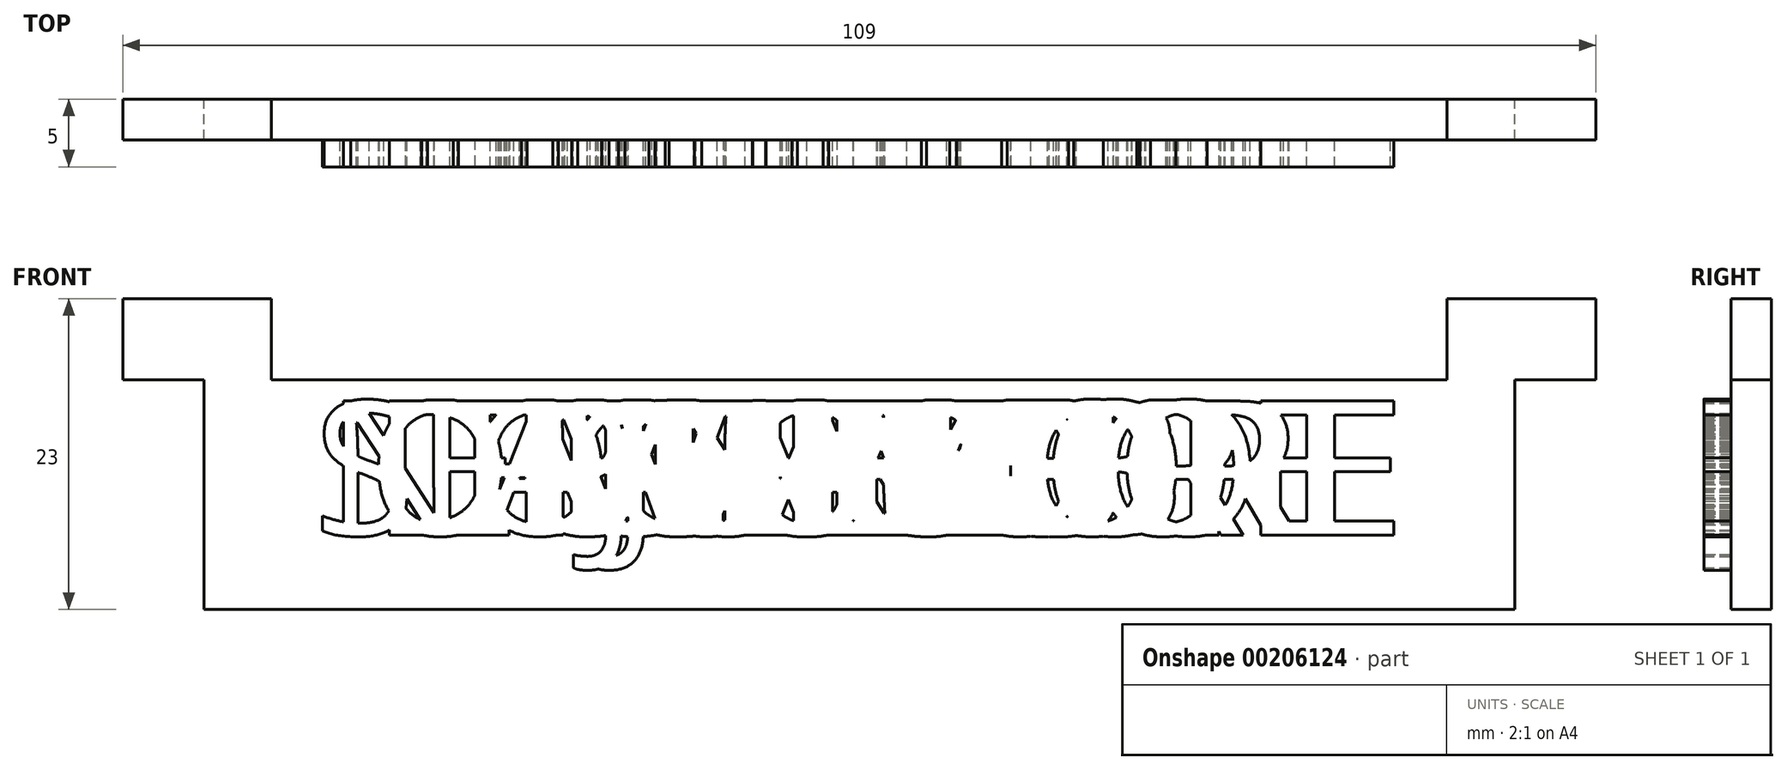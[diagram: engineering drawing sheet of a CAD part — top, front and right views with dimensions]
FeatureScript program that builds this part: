
annotation { "Feature Type Name" : "Feature", "Feature Type Description" : "" }
export const myFeature = defineFeature(function(context is Context, id is Id, definition is map)
    precondition{}
    {
        {
            var Q0;
            Q0=qCreatedBy(makeId("Front.planeOp"),FACE);
            var sketch = newSketch(context, id + "F0", { "sketchPlane" : qUnion([Q0])});
            skLineSegment(sketch, "E0.bottom", {"start": v(-51.5, 23) * mm, "end": v(-40.5, 23) * mm});
            skLineSegment(sketch, "E0.top", {"start": v(-45.5, 0) * mm, "end": v(51.5, 0) * mm});
            skLineSegment(sketch, "E0.left", {"start": v(-51.5, 23) * mm, "end": v(-51.5, 17) * mm});
            skLineSegment(sketch, "E0.right", {"start": v(57.5, 23) * mm, "end": v(57.5, 17) * mm});
            skLineSegment(sketch, "E1.top", {"start": v(-51.5, 17) * mm, "end": v(-45.5, 17) * mm});
            skLineSegment(sketch, "E1.right", {"start": v(-45.5, 0) * mm, "end": v(-45.5, 17) * mm});
            skLineSegment(sketch, "E2.bottom", {"start": v(-51.5, 23) * mm, "end": v(-40.5, 23) * mm, "construction": true});
            skLineSegment(sketch, "E2.top", {"start": v(-51.5, 17) * mm, "end": v(-40.5, 17) * mm, "construction": true});
            skLineSegment(sketch, "E2.left", {"start": v(-51.5, 23) * mm, "end": v(-51.5, 17) * mm, "construction": true});
            skLineSegment(sketch, "E2.right", {"start": v(-40.5, 23) * mm, "end": v(-40.5, 17) * mm, "construction": true});
            skLineSegment(sketch, "E3.top", {"start": v(-40.5, 17) * mm, "end": v(46.5, 17) * mm});
            skLineSegment(sketch, "E3.left", {"start": v(-40.5, 23) * mm, "end": v(-40.5, 17) * mm});
            skLineSegment(sketch, "E3.right", {"start": v(46.5, 23) * mm, "end": v(46.5, 17) * mm});
            skLineSegment(sketch, "E4.top", {"start": v(57.5, 17) * mm, "end": v(51.5, 17) * mm});
            skLineSegment(sketch, "E4.right", {"start": v(51.5, 0) * mm, "end": v(51.5, 17) * mm});
            skLineSegment(sketch, "E5.trimOffspring", {"start": v(46.5, 23) * mm, "end": v(57.5, 23) * mm});
            skSolve(sketch);
        }
        {
            var Q0;
            Q0=makeQuery(id+"F0.imprint","IMPRINT",FACE,{"disambiguationData":[TD([[makeQuery(id+"F0.imprint","IMPRINT",EDGE,{"derivedFrom":sQuery(id+"F0.wireOp",EDGE,"E0.bottom")}),-1.0]])]});
            extrude(context, id + "F1", {"entities" : qUnion([Q0]), "depth" : 3 * mm});
        }
        {
            var Q0;
            Q0=makeQuery(id+"F1.opExtrude","CAP_FACE",FACE,{"disambiguationData":[OSD([sQuery(id+"F0.wireOp",EDGE,"E0.bottom"),sQuery(id+"F0.wireOp",EDGE,"E0.top"),sQuery(id+"F0.wireOp",EDGE,"E0.left"),sQuery(id+"F0.wireOp",EDGE,"E0.right"),sQuery(id+"F0.wireOp",EDGE,"E1.top"),sQuery(id+"F0.wireOp",EDGE,"E1.right"),sQuery(id+"F0.wireOp",EDGE,"E3.top"),sQuery(id+"F0.wireOp",EDGE,"E3.left"),sQuery(id+"F0.wireOp",EDGE,"E3.right"),sQuery(id+"F0.wireOp",EDGE,"E4.top"),sQuery(id+"F0.wireOp",EDGE,"E4.right"),sQuery(id+"F0.wireOp",EDGE,"E5.trimOffspring")])],"isStart":false});
            var sketch = newSketch(context, id + "F2", { "sketchPlane" : qUnion([Q0])});
            skLineSegment(sketch, "E6.0", {"start": v(-45.5, 3.5) * mm, "end": v(-42, 3.5) * mm, "construction": true});
            skLineSegment(sketch, "E7.0", {"start": v(-42, 15.5) * mm, "end": v(48, 15.5) * mm, "construction": true});
            skLineSegment(sketch, "E8.0", {"start": v(-42, 0) * mm, "end": v(-42, 15.5) * mm, "construction": true});
            skText(sketch, "E9", { "text": "ENERO", "fontName": "OpenSans-Regular.ttf"});
            skLineSegment(sketch, "E10.top", {"start": v(-45.5, 0) * mm, "end": v(-42, 0) * mm, "construction": true});
            skLineSegment(sketch, "E10.left", {"start": v(-45.5, 3.5) * mm, "end": v(-45.5, 0) * mm, "construction": true});
            skLineSegment(sketch, "E10.right", {"start": v(-42, 3.5) * mm, "end": v(-42, 0) * mm, "construction": true});
            skLineSegment(sketch, "E11.0", {"start": v(48, 0) * mm, "end": v(48, 17) * mm, "construction": true});
            skPoint(sketch, "E12.orphan", {"position": v(48, 15.5) * mm});
            skPoint(sketch, "E13.end.orphan", {"position": v(3, 0) * mm});
            skLineSegment(sketch, "E14", {"start": v(3, 17) * mm, "end": v(3, 0) * mm, "construction": true});
            const initialGuessF2  = {"E9": [-0.01969, 0.0055, 1, 0, 0.01]};
            skSetInitialGuess(sketch, initialGuessF2);
            skSolve(sketch);
        }
        {
            var Q0;
            Q0=makeQuery(id+"F2.imprint","IMPRINT",FACE,{"disambiguationData":[TD([[makeQuery(id+"F2.imprint","IMPRINT",EDGE,{"derivedFrom":sQuery(id+"F2.wireOp",EDGE,"E9.sketch_text.stroke-0")}),-1.0]])]});
            var Q1;
            Q1=makeQuery(id+"F2.imprint","IMPRINT",FACE,{"disambiguationData":[TD([[makeQuery(id+"F2.imprint","IMPRINT",EDGE,{"derivedFrom":sQuery(id+"F2.wireOp",EDGE,"E9.sketch_text.stroke-10")}),-1.0]])]});
            var Q2;
            Q2=makeQuery(id+"F2.imprint","IMPRINT",FACE,{"disambiguationData":[TD([[makeQuery(id+"F2.imprint","IMPRINT",EDGE,{"derivedFrom":sQuery(id+"F2.wireOp",EDGE,"E9.sketch_text.stroke-23")}),-1.0]])]});
            var Q3;
            Q3=makeQuery(id+"F2.imprint","IMPRINT",FACE,{"disambiguationData":[TD([[makeQuery(id+"F2.imprint","IMPRINT",EDGE,{"derivedFrom":sQuery(id+"F2.wireOp",EDGE,"E9.sketch_text.stroke-38")}),-1.0]])]});
            var Q4;
            Q4=makeQuery(id+"F2.imprint","IMPRINT",FACE,{"disambiguationData":[TD([[makeQuery(id+"F2.imprint","IMPRINT",EDGE,{"derivedFrom":sQuery(id+"F2.wireOp",EDGE,"E9.sketch_text.stroke-52")}),-1.0]])]});
            var Q5;
            Q5=makeQuery(id+"F2.imprint","IMPRINT",FACE,{"disambiguationData":[TD([[makeQuery(id+"F2.imprint","IMPRINT",EDGE,{"derivedFrom":sQuery(id+"F2.wireOp",EDGE,"E9.sketch_text.stroke-65")}),-1.0]])]});
            var Q6;
            Q6=makeQuery(id+"F2.imprint","IMPRINT",FACE,{"disambiguationData":[TD([[makeQuery(id+"F2.imprint","IMPRINT",EDGE,{"derivedFrom":sQuery(id+"F2.wireOp",EDGE,"E9.sketch_text.stroke-83")}),-1.0]])]});
            extrude(context, id + "F3", {"entities" : qUnion([Q0, Q1, Q2, Q3, Q4, Q5, Q6]), "operationType" : NewBodyOperationType.ADD, "depth" : 2 * mm});
        }
        {
            var Q0;
            Q0=qSketchRegion(id+"F0",true);
            extrude(context, id + "F4", {"entities" : qUnion([Q0]), "depth" : 3 * mm});
        }
        {
            var Q0;
            Q0=makeQuery(id+"F4.opExtrude","CAP_FACE",FACE,{"disambiguationData":[OSD([sQuery(id+"F0.wireOp",EDGE,"E0.bottom"),sQuery(id+"F0.wireOp",EDGE,"E0.top"),sQuery(id+"F0.wireOp",EDGE,"E0.left"),sQuery(id+"F0.wireOp",EDGE,"E0.right"),sQuery(id+"F0.wireOp",EDGE,"E1.top"),sQuery(id+"F0.wireOp",EDGE,"E1.right"),sQuery(id+"F0.wireOp",EDGE,"E3.top"),sQuery(id+"F0.wireOp",EDGE,"E3.left"),sQuery(id+"F0.wireOp",EDGE,"E3.right"),sQuery(id+"F0.wireOp",EDGE,"E4.top"),sQuery(id+"F0.wireOp",EDGE,"E4.right"),sQuery(id+"F0.wireOp",EDGE,"E5.trimOffspring")])],"isStart":false});
            var sketch = newSketch(context, id + "F5", { "sketchPlane" : qUnion([Q0])});
            skText(sketch, "E15", { "text": "FEBRERO", "fontName": "OpenSans-Regular.ttf"});
            skPoint(sketch, "E16.orphan", {"position": v(44.22, 15.5) * mm});
            skPoint(sketch, "E17.end.orphan", {"position": v(-0.5, 0) * mm});
            skPoint(sketch, "E18.orphan", {"position": v(-38.22, 15.5) * mm});
            skLineSegment(sketch, "E19.0", {"start": v(-43.5, 15.5) * mm, "end": v(49.5, 15.5) * mm, "construction": true});
            skPoint(sketch, "E20.start.orphan", {"position": v(3, 17) * mm});
            const initialGuessF5  = {"E15": [-0.02683, 0.0055, 1, 0, 0.01]};
            skSetInitialGuess(sketch, initialGuessF5);
            skSolve(sketch);
        }
        {
            var Q0;
            Q0=makeQuery(id+"F5.imprint","IMPRINT",FACE,{"disambiguationData":[TD([[makeQuery(id+"F5.imprint","IMPRINT",EDGE,{"derivedFrom":sQuery(id+"F5.wireOp",EDGE,"E15.sketch_text.stroke-0")}),-1.0]])]});
            var Q1;
            Q1=makeQuery(id+"F5.imprint","IMPRINT",FACE,{"disambiguationData":[TD([[makeQuery(id+"F5.imprint","IMPRINT",EDGE,{"derivedFrom":sQuery(id+"F5.wireOp",EDGE,"E15.sketch_text.stroke-10")}),-1.0]])]});
            var Q2;
            Q2=makeQuery(id+"F5.imprint","IMPRINT",FACE,{"disambiguationData":[TD([[makeQuery(id+"F5.imprint","IMPRINT",EDGE,{"derivedFrom":sQuery(id+"F5.wireOp",EDGE,"E15.sketch_text.stroke-22")}),-1.0]])]});
            var Q3;
            Q3=makeQuery(id+"F5.imprint","IMPRINT",FACE,{"disambiguationData":[TD([[makeQuery(id+"F5.imprint","IMPRINT",EDGE,{"derivedFrom":sQuery(id+"F5.wireOp",EDGE,"E15.sketch_text.stroke-47")}),-1.0]])]});
            var Q4;
            Q4=makeQuery(id+"F5.imprint","IMPRINT",FACE,{"disambiguationData":[TD([[makeQuery(id+"F5.imprint","IMPRINT",EDGE,{"derivedFrom":sQuery(id+"F5.wireOp",EDGE,"E15.sketch_text.stroke-65")}),-1.0]])]});
            var Q5;
            Q5=makeQuery(id+"F5.imprint","IMPRINT",FACE,{"disambiguationData":[TD([[makeQuery(id+"F5.imprint","IMPRINT",EDGE,{"derivedFrom":sQuery(id+"F5.wireOp",EDGE,"E15.sketch_text.stroke-79")}),-1.0]])]});
            var Q6;
            Q6=makeQuery(id+"F5.imprint","IMPRINT",FACE,{"disambiguationData":[TD([[makeQuery(id+"F5.imprint","IMPRINT",EDGE,{"derivedFrom":sQuery(id+"F5.wireOp",EDGE,"E15.sketch_text.stroke-92")}),-1.0]])]});
            var Q7;
            Q7=makeQuery(id+"F5.imprint","IMPRINT",FACE,{"disambiguationData":[TD([[makeQuery(id+"F5.imprint","IMPRINT",EDGE,{"derivedFrom":sQuery(id+"F5.wireOp",EDGE,"E15.sketch_text.stroke-110")}),-1.0]])]});
            extrude(context, id + "F6", {"entities" : qUnion([Q0, Q1, Q2, Q3, Q4, Q5, Q6, Q7]), "operationType" : NewBodyOperationType.ADD, "depth" : 2 * mm});
        }
        {
            var Q0;
            Q0=makeQuery(id+"F0.imprint","IMPRINT",FACE,{"disambiguationData":[TD([[makeQuery(id+"F0.imprint","IMPRINT",EDGE,{"derivedFrom":sQuery(id+"F0.wireOp",EDGE,"E0.bottom")}),-1.0]])]});
            extrude(context, id + "F7", {"entities" : qUnion([Q0]), "depth" : 3 * mm});
        }
        {
            var Q0;
            Q0=makeQuery(id+"F7.opExtrude","CAP_FACE",FACE,{"disambiguationData":[OSD([sQuery(id+"F0.wireOp",EDGE,"E0.bottom"),sQuery(id+"F0.wireOp",EDGE,"E0.top"),sQuery(id+"F0.wireOp",EDGE,"E0.left"),sQuery(id+"F0.wireOp",EDGE,"E0.right"),sQuery(id+"F0.wireOp",EDGE,"E1.top"),sQuery(id+"F0.wireOp",EDGE,"E1.right"),sQuery(id+"F0.wireOp",EDGE,"E3.top"),sQuery(id+"F0.wireOp",EDGE,"E3.left"),sQuery(id+"F0.wireOp",EDGE,"E3.right"),sQuery(id+"F0.wireOp",EDGE,"E4.top"),sQuery(id+"F0.wireOp",EDGE,"E4.right"),sQuery(id+"F0.wireOp",EDGE,"E5.trimOffspring")])],"isStart":false});
            var sketch = newSketch(context, id + "F8", { "sketchPlane" : qUnion([Q0])});
            skText(sketch, "E21", { "text": "MARZO", "fontName": "OpenSans-Regular.ttf"});
            skPoint(sketch, "E22.orphan", {"position": v(38.75, 15.5) * mm});
            skPoint(sketch, "E23.end.orphan", {"position": v(0, -12.7) * mm});
            skPoint(sketch, "E24.orphan", {"position": v(-32.75, 15.5) * mm});
            skPoint(sketch, "E25.start.orphan", {"position": v(0, 4.3) * mm});
            skLineSegment(sketch, "E26.0", {"start": v(-43.5, 15.5) * mm, "end": v(49.5, 15.5) * mm, "construction": true});
            const initialGuessF8  = {"E21": [-0.02136, 0.0055, 1, 0, 0.01]};
            skSetInitialGuess(sketch, initialGuessF8);
            skSolve(sketch);
        }
        {
            var Q0;
            Q0=makeQuery(id+"F8.imprint","IMPRINT",FACE,{"disambiguationData":[TD([[makeQuery(id+"F8.imprint","IMPRINT",EDGE,{"derivedFrom":sQuery(id+"F8.wireOp",EDGE,"E21.sketch_text.stroke-0")}),-1.0]])]});
            var Q1;
            Q1=makeQuery(id+"F8.imprint","IMPRINT",FACE,{"disambiguationData":[TD([[makeQuery(id+"F8.imprint","IMPRINT",EDGE,{"derivedFrom":sQuery(id+"F8.wireOp",EDGE,"E21.sketch_text.stroke-18")}),-1.0]])]});
            var Q2;
            Q2=makeQuery(id+"F8.imprint","IMPRINT",FACE,{"disambiguationData":[TD([[makeQuery(id+"F8.imprint","IMPRINT",EDGE,{"derivedFrom":sQuery(id+"F8.wireOp",EDGE,"E21.sketch_text.stroke-31")}),-1.0]])]});
            var Q3;
            Q3=makeQuery(id+"F8.imprint","IMPRINT",FACE,{"disambiguationData":[TD([[makeQuery(id+"F8.imprint","IMPRINT",EDGE,{"derivedFrom":sQuery(id+"F8.wireOp",EDGE,"E21.sketch_text.stroke-49")}),-1.0]])]});
            var Q4;
            Q4=makeQuery(id+"F8.imprint","IMPRINT",FACE,{"disambiguationData":[TD([[makeQuery(id+"F8.imprint","IMPRINT",EDGE,{"derivedFrom":sQuery(id+"F8.wireOp",EDGE,"E21.sketch_text.stroke-64")}),-1.0]])]});
            extrude(context, id + "F9", {"entities" : qUnion([Q0, Q1, Q2, Q3, Q4]), "operationType" : NewBodyOperationType.ADD, "depth" : 2 * mm});
        }
        {
            var Q0;
            Q0=makeQuery(id+"F0.imprint","IMPRINT",FACE,{"disambiguationData":[TD([[makeQuery(id+"F0.imprint","IMPRINT",EDGE,{"derivedFrom":sQuery(id+"F0.wireOp",EDGE,"E0.bottom")}),-1.0]])]});
            extrude(context, id + "F10", {"entities" : qUnion([Q0]), "depth" : 3 * mm});
        }
        {
            var Q0;
            Q0=makeQuery(id+"F10.opExtrude","CAP_FACE",FACE,{"disambiguationData":[OSD([sQuery(id+"F0.wireOp",EDGE,"E0.bottom"),sQuery(id+"F0.wireOp",EDGE,"E0.top"),sQuery(id+"F0.wireOp",EDGE,"E0.left"),sQuery(id+"F0.wireOp",EDGE,"E0.right"),sQuery(id+"F0.wireOp",EDGE,"E1.top"),sQuery(id+"F0.wireOp",EDGE,"E1.right"),sQuery(id+"F0.wireOp",EDGE,"E3.top"),sQuery(id+"F0.wireOp",EDGE,"E3.left"),sQuery(id+"F0.wireOp",EDGE,"E3.right"),sQuery(id+"F0.wireOp",EDGE,"E4.top"),sQuery(id+"F0.wireOp",EDGE,"E4.right"),sQuery(id+"F0.wireOp",EDGE,"E5.trimOffspring")])],"isStart":false});
            var sketch = newSketch(context, id + "F11", { "sketchPlane" : qUnion([Q0])});
            skText(sketch, "E27", { "text": "ABRIL", "fontName": "OpenSans-Regular.ttf"});
            skPoint(sketch, "E28.orphan", {"position": v(33.4, 15.5) * mm});
            skPoint(sketch, "E29.end.orphan", {"position": v(0.3, -20.32) * mm});
            skPoint(sketch, "E30.orphan", {"position": v(-27.4, 15.5) * mm});
            skPoint(sketch, "E31.start.orphan", {"position": v(0.3, -3.32) * mm});
            skLineSegment(sketch, "E32.0", {"start": v(-43.5, 15.5) * mm, "end": v(49.5, 15.5) * mm});
            const initialGuessF11  = {"E27": [-0.01602, 0.0055, 1, 0, 0.01]};
            skSetInitialGuess(sketch, initialGuessF11);
            skSolve(sketch);
        }
        {
            var Q0;
            Q0=makeQuery(id+"F11.imprint","IMPRINT",FACE,{"disambiguationData":[TD([[makeQuery(id+"F11.imprint","IMPRINT",EDGE,{"derivedFrom":sQuery(id+"F11.wireOp",EDGE,"E27.sketch_text.stroke-0")}),-1.0]])]});
            var Q1;
            Q1=makeQuery(id+"F11.imprint","IMPRINT",FACE,{"disambiguationData":[TD([[makeQuery(id+"F11.imprint","IMPRINT",EDGE,{"derivedFrom":sQuery(id+"F11.wireOp",EDGE,"E27.sketch_text.stroke-13")}),-1.0]])]});
            var Q2;
            Q2=makeQuery(id+"F11.imprint","IMPRINT",FACE,{"disambiguationData":[TD([[makeQuery(id+"F11.imprint","IMPRINT",EDGE,{"derivedFrom":sQuery(id+"F11.wireOp",EDGE,"E27.sketch_text.stroke-28")}),-1.0]])]});
            var Q3;
            Q3=makeQuery(id+"F11.imprint","IMPRINT",FACE,{"disambiguationData":[TD([[makeQuery(id+"F11.imprint","IMPRINT",EDGE,{"derivedFrom":sQuery(id+"F11.wireOp",EDGE,"E27.sketch_text.stroke-46")}),-1.0]])]});
            var Q4;
            Q4=makeQuery(id+"F11.imprint","IMPRINT",FACE,{"disambiguationData":[TD([[makeQuery(id+"F11.imprint","IMPRINT",EDGE,{"derivedFrom":sQuery(id+"F11.wireOp",EDGE,"E27.sketch_text.stroke-50")}),-1.0]])]});
            var Q5;
            Q5=makeQuery(id+"F11.imprint","IMPRINT",FACE,{"disambiguationData":[TD([[makeQuery(id+"F11.imprint","IMPRINT",EDGE,{"derivedFrom":sQuery(id+"F11.wireOp",EDGE,"E27.sketch_text.stroke-56")}),-1.0]])]});
            var Q6;
            Q6=makeQuery(id+"F11.imprint","IMPRINT",FACE,{"disambiguationData":[TD([[makeQuery(id+"F11.imprint","IMPRINT",EDGE,{"derivedFrom":sQuery(id+"F11.wireOp",EDGE,"E27.sketch_text.stroke-60")}),-1.0]])]});
            extrude(context, id + "F12", {"entities" : qUnion([Q0, Q1, Q2, Q3, Q4, Q5, Q6]), "operationType" : NewBodyOperationType.ADD, "depth" : 2 * mm});
        }
        {
            var Q0;
            Q0=makeQuery(id+"F0.imprint","IMPRINT",FACE,{"disambiguationData":[TD([[makeQuery(id+"F0.imprint","IMPRINT",EDGE,{"derivedFrom":sQuery(id+"F0.wireOp",EDGE,"E0.bottom")}),-1.0]])]});
            extrude(context, id + "F13", {"entities" : qUnion([Q0]), "depth" : 3 * mm});
        }
        {
            var Q0;
            Q0=makeQuery(id+"F13.opExtrude","CAP_FACE",FACE,{"disambiguationData":[OSD([sQuery(id+"F0.wireOp",EDGE,"E0.bottom"),sQuery(id+"F0.wireOp",EDGE,"E0.top"),sQuery(id+"F0.wireOp",EDGE,"E0.left"),sQuery(id+"F0.wireOp",EDGE,"E0.right"),sQuery(id+"F0.wireOp",EDGE,"E1.top"),sQuery(id+"F0.wireOp",EDGE,"E1.right"),sQuery(id+"F0.wireOp",EDGE,"E3.top"),sQuery(id+"F0.wireOp",EDGE,"E3.left"),sQuery(id+"F0.wireOp",EDGE,"E3.right"),sQuery(id+"F0.wireOp",EDGE,"E4.top"),sQuery(id+"F0.wireOp",EDGE,"E4.right"),sQuery(id+"F0.wireOp",EDGE,"E5.trimOffspring")])],"isStart":false});
            var sketch = newSketch(context, id + "F14", { "sketchPlane" : qUnion([Q0])});
            skText(sketch, "E33", { "text": "MAYO", "fontName": "OpenSans-Regular.ttf"});
            skPoint(sketch, "E34.orphan", {"position": v(34.38, 15.5) * mm});
            skPoint(sketch, "E35.end.orphan", {"position": v(0.48, -24.9) * mm});
            skPoint(sketch, "E36.orphan", {"position": v(-28.38, 15.5) * mm});
            skPoint(sketch, "E37.start.orphan", {"position": v(0.48, -7.9) * mm});
            skLineSegment(sketch, "E38.0", {"start": v(-41.29, 15.5) * mm, "end": v(47.29, 15.5) * mm});
            skLineSegment(sketch, "E39.0", {"start": v(-43.5, 15.5) * mm, "end": v(49.5, 15.5) * mm});
            const initialGuessF14  = {"E33": [-0.01699, 0.0055, 1, 0, 0.01]};
            skSetInitialGuess(sketch, initialGuessF14);
            skSolve(sketch);
        }
        {
            var Q0;
            Q0=makeQuery(id+"F0.imprint","IMPRINT",FACE,{"disambiguationData":[TD([[makeQuery(id+"F0.imprint","IMPRINT",EDGE,{"derivedFrom":sQuery(id+"F0.wireOp",EDGE,"E0.bottom")}),-1.0]])]});
            extrude(context, id + "F15", {"entities" : qUnion([Q0]), "depth" : 3 * mm});
        }
        {
            var Q0;
            Q0=makeQuery(id+"F15.opExtrude","CAP_FACE",FACE,{"disambiguationData":[OSD([sQuery(id+"F0.wireOp",EDGE,"E0.bottom"),sQuery(id+"F0.wireOp",EDGE,"E0.top"),sQuery(id+"F0.wireOp",EDGE,"E0.left"),sQuery(id+"F0.wireOp",EDGE,"E0.right"),sQuery(id+"F0.wireOp",EDGE,"E1.top"),sQuery(id+"F0.wireOp",EDGE,"E1.right"),sQuery(id+"F0.wireOp",EDGE,"E3.top"),sQuery(id+"F0.wireOp",EDGE,"E3.left"),sQuery(id+"F0.wireOp",EDGE,"E3.right"),sQuery(id+"F0.wireOp",EDGE,"E4.top"),sQuery(id+"F0.wireOp",EDGE,"E4.right"),sQuery(id+"F0.wireOp",EDGE,"E5.trimOffspring")])],"isStart":false});
            var sketch = newSketch(context, id + "F16", { "sketchPlane" : qUnion([Q0])});
            skText(sketch, "E40", { "text": "JUNIO", "fontName": "OpenSans-Regular.ttf"});
            skPoint(sketch, "E41.orphan", {"position": v(34.45, 15.5) * mm});
            skPoint(sketch, "E42.end.orphan", {"position": v(0.65, -29.76) * mm});
            skPoint(sketch, "E43.orphan", {"position": v(-28.45, 15.5) * mm});
            skPoint(sketch, "E44.start.orphan", {"position": v(0.65, -12.76) * mm});
            skLineSegment(sketch, "E45.0", {"start": v(-41.36, 15.5) * mm, "end": v(47.36, 15.5) * mm});
            skLineSegment(sketch, "E46.0", {"start": v(-45.06, 15.5) * mm, "end": v(51.06, 15.5) * mm});
            skLineSegment(sketch, "E47.0", {"start": v(-43.5, 15.5) * mm, "end": v(49.5, 15.5) * mm});
            const initialGuessF16  = {"E40": [-0.01706, 0.0055, 1, 0, 0.01]};
            skSetInitialGuess(sketch, initialGuessF16);
            skSolve(sketch);
        }
        {
            var Q0;
            Q0=makeQuery(id+"F0.imprint","IMPRINT",FACE,{"disambiguationData":[TD([[makeQuery(id+"F0.imprint","IMPRINT",EDGE,{"derivedFrom":sQuery(id+"F0.wireOp",EDGE,"E0.bottom")}),-1.0]])]});
            extrude(context, id + "F17", {"entities" : qUnion([Q0]), "depth" : 3 * mm});
        }
        {
            var Q0;
            Q0=makeQuery(id+"F17.opExtrude","CAP_FACE",FACE,{"disambiguationData":[OSD([sQuery(id+"F0.wireOp",EDGE,"E0.bottom"),sQuery(id+"F0.wireOp",EDGE,"E0.top"),sQuery(id+"F0.wireOp",EDGE,"E0.left"),sQuery(id+"F0.wireOp",EDGE,"E0.right"),sQuery(id+"F0.wireOp",EDGE,"E1.top"),sQuery(id+"F0.wireOp",EDGE,"E1.right"),sQuery(id+"F0.wireOp",EDGE,"E3.top"),sQuery(id+"F0.wireOp",EDGE,"E3.left"),sQuery(id+"F0.wireOp",EDGE,"E3.right"),sQuery(id+"F0.wireOp",EDGE,"E4.top"),sQuery(id+"F0.wireOp",EDGE,"E4.right"),sQuery(id+"F0.wireOp",EDGE,"E5.trimOffspring")])],"isStart":false});
            var sketch = newSketch(context, id + "F18", { "sketchPlane" : qUnion([Q0])});
            skText(sketch, "E48", { "text": "JULIO", "fontName": "OpenSans-Regular.ttf"});
            skPoint(sketch, "E49.orphan", {"position": v(32.82, 15.5) * mm});
            skPoint(sketch, "E50.end.orphan", {"position": v(0.82, -34.76) * mm});
            skPoint(sketch, "E51.orphan", {"position": v(-26.82, 15.5) * mm});
            skPoint(sketch, "E52.start.orphan", {"position": v(0.82, -17.76) * mm});
            skLineSegment(sketch, "E53.0", {"start": v(-39.73, 15.5) * mm, "end": v(45.73, 15.5) * mm});
            skLineSegment(sketch, "E54.0", {"start": v(-43.42, 15.5) * mm, "end": v(49.42, 15.5) * mm});
            skLineSegment(sketch, "E55.0", {"start": v(-41.84, 15.5) * mm, "end": v(47.84, 15.5) * mm});
            skLineSegment(sketch, "E56.0", {"start": v(-43.5, 15.5) * mm, "end": v(49.5, 15.5) * mm});
            const initialGuessF18  = {"E48": [-0.01543, 0.0055, 1, 0, 0.01]};
            skSetInitialGuess(sketch, initialGuessF18);
            skSolve(sketch);
        }
        {
            var Q0;
            Q0=makeQuery(id+"F0.imprint","IMPRINT",FACE,{"disambiguationData":[TD([[makeQuery(id+"F0.imprint","IMPRINT",EDGE,{"derivedFrom":sQuery(id+"F0.wireOp",EDGE,"E0.bottom")}),-1.0]])]});
            extrude(context, id + "F19", {"entities" : qUnion([Q0]), "depth" : 3 * mm});
        }
        {
            var Q0;
            Q0=makeQuery(id+"F19.opExtrude","CAP_FACE",FACE,{"disambiguationData":[OSD([sQuery(id+"F0.wireOp",EDGE,"E0.bottom"),sQuery(id+"F0.wireOp",EDGE,"E0.top"),sQuery(id+"F0.wireOp",EDGE,"E0.left"),sQuery(id+"F0.wireOp",EDGE,"E0.right"),sQuery(id+"F0.wireOp",EDGE,"E1.top"),sQuery(id+"F0.wireOp",EDGE,"E1.right"),sQuery(id+"F0.wireOp",EDGE,"E3.top"),sQuery(id+"F0.wireOp",EDGE,"E3.left"),sQuery(id+"F0.wireOp",EDGE,"E3.right"),sQuery(id+"F0.wireOp",EDGE,"E4.top"),sQuery(id+"F0.wireOp",EDGE,"E4.right"),sQuery(id+"F0.wireOp",EDGE,"E5.trimOffspring")])],"isStart":false});
            var sketch = newSketch(context, id + "F20", { "sketchPlane" : qUnion([Q0])});
            skText(sketch, "E57", { "text": "AGOSTO", "fontName": "OpenSans-Regular.ttf"});
            skPoint(sketch, "E58.orphan", {"position": v(42.34, 15.5) * mm});
            skPoint(sketch, "E59.end.orphan", {"position": v(1, -39.82) * mm});
            skPoint(sketch, "E60.orphan", {"position": v(-36.34, 15.5) * mm});
            skPoint(sketch, "E61.start.orphan", {"position": v(1, -22.82) * mm});
            skLineSegment(sketch, "E62.0", {"start": v(-49.25, 15.5) * mm, "end": v(55.25, 15.5) * mm});
            skLineSegment(sketch, "E63.0", {"start": v(-52.94, 15.5) * mm, "end": v(58.94, 15.5) * mm});
            skLineSegment(sketch, "E64.0", {"start": v(-51.36, 15.5) * mm, "end": v(57.36, 15.5) * mm});
            skLineSegment(sketch, "E65.0", {"start": v(-52.55, 15.5) * mm, "end": v(58.55, 15.5) * mm});
            skLineSegment(sketch, "E66.0", {"start": v(-43.5, 15.5) * mm, "end": v(49.5, 15.5) * mm});
            const initialGuessF20  = {"E57": [-0.02495, 0.0055, 1, 0, 0.01]};
            skSetInitialGuess(sketch, initialGuessF20);
            skSolve(sketch);
        }
        {
            var Q0;
            Q0=makeQuery(id+"F0.imprint","IMPRINT",FACE,{"disambiguationData":[TD([[makeQuery(id+"F0.imprint","IMPRINT",EDGE,{"derivedFrom":sQuery(id+"F0.wireOp",EDGE,"E0.bottom")}),-1.0]])]});
            extrude(context, id + "F21", {"entities" : qUnion([Q0]), "depth" : 3 * mm});
        }
        {
            var Q0;
            Q0=makeQuery(id+"F21.opExtrude","CAP_FACE",FACE,{"disambiguationData":[OSD([sQuery(id+"F0.wireOp",EDGE,"E0.bottom"),sQuery(id+"F0.wireOp",EDGE,"E0.top"),sQuery(id+"F0.wireOp",EDGE,"E0.left"),sQuery(id+"F0.wireOp",EDGE,"E0.right"),sQuery(id+"F0.wireOp",EDGE,"E1.top"),sQuery(id+"F0.wireOp",EDGE,"E1.right"),sQuery(id+"F0.wireOp",EDGE,"E3.top"),sQuery(id+"F0.wireOp",EDGE,"E3.left"),sQuery(id+"F0.wireOp",EDGE,"E3.right"),sQuery(id+"F0.wireOp",EDGE,"E4.top"),sQuery(id+"F0.wireOp",EDGE,"E4.right"),sQuery(id+"F0.wireOp",EDGE,"E5.trimOffspring")])],"isStart":false});
            var sketch = newSketch(context, id + "F22", { "sketchPlane" : qUnion([Q0])});
            skText(sketch, "E67", { "text": "SEPTIEMBRE", "fontName": "OpenSans-Regular.ttf"});
            skPoint(sketch, "E68.orphan", {"position": v(54.84, 15.5) * mm});
            skPoint(sketch, "E69.end.orphan", {"position": v(1.16, -44.91) * mm});
            skPoint(sketch, "E70.orphan", {"position": v(-48.84, 15.5) * mm});
            skPoint(sketch, "E71.start.orphan", {"position": v(1.16, -27.91) * mm});
            const initialGuessF22  = {"E67": [-0.03745, 0.0055, 1, 0, 0.01]};
            skSetInitialGuess(sketch, initialGuessF22);
            skSolve(sketch);
        }
        {
            var Q0;
            Q0=makeQuery(id+"F0.imprint","IMPRINT",FACE,{"disambiguationData":[TD([[makeQuery(id+"F0.imprint","IMPRINT",EDGE,{"derivedFrom":sQuery(id+"F0.wireOp",EDGE,"E0.bottom")}),-1.0]])]});
            extrude(context, id + "F23", {"entities" : qUnion([Q0]), "depth" : 3 * mm});
        }
        {
            var Q0;
            Q0=makeQuery(id+"F23.opExtrude","CAP_FACE",FACE,{"disambiguationData":[OSD([sQuery(id+"F0.wireOp",EDGE,"E0.bottom"),sQuery(id+"F0.wireOp",EDGE,"E0.top"),sQuery(id+"F0.wireOp",EDGE,"E0.left"),sQuery(id+"F0.wireOp",EDGE,"E0.right"),sQuery(id+"F0.wireOp",EDGE,"E1.top"),sQuery(id+"F0.wireOp",EDGE,"E1.right"),sQuery(id+"F0.wireOp",EDGE,"E3.top"),sQuery(id+"F0.wireOp",EDGE,"E3.left"),sQuery(id+"F0.wireOp",EDGE,"E3.right"),sQuery(id+"F0.wireOp",EDGE,"E4.top"),sQuery(id+"F0.wireOp",EDGE,"E4.right"),sQuery(id+"F0.wireOp",EDGE,"E5.trimOffspring")])],"isStart":false});
            var sketch = newSketch(context, id + "F24", { "sketchPlane" : qUnion([Q0])});
            skText(sketch, "E72", { "text": "OCTUBURE", "fontName": "OpenSans-Regular.ttf"});
            skPoint(sketch, "E73.orphan", {"position": v(50.82, 15.5) * mm});
            skPoint(sketch, "E74.end.orphan", {"position": v(1.08, -34.46) * mm});
            skPoint(sketch, "E75.orphan", {"position": v(-44.82, 15.5) * mm});
            skPoint(sketch, "E76.start.orphan", {"position": v(1.08, -17.46) * mm});
            skLineSegment(sketch, "E77.0", {"start": v(-42.5, 15.5) * mm, "end": v(48.5, 15.5) * mm});
            const initialGuessF24  = {"E72": [-0.03343, 0.0055, 1, 0, 0.01]};
            skSetInitialGuess(sketch, initialGuessF24);
            skSolve(sketch);
        }
        {
            var Q0;
            Q0=makeQuery(id+"F0.imprint","IMPRINT",FACE,{"disambiguationData":[TD([[makeQuery(id+"F0.imprint","IMPRINT",EDGE,{"derivedFrom":sQuery(id+"F0.wireOp",EDGE,"E0.bottom")}),-1.0]])]});
            extrude(context, id + "F25", {"entities" : qUnion([Q0]), "depth" : 3 * mm});
        }
        {
            var Q0;
            Q0=makeQuery(id+"F25.opExtrude","CAP_FACE",FACE,{"disambiguationData":[OSD([sQuery(id+"F0.wireOp",EDGE,"E0.bottom"),sQuery(id+"F0.wireOp",EDGE,"E0.top"),sQuery(id+"F0.wireOp",EDGE,"E0.left"),sQuery(id+"F0.wireOp",EDGE,"E0.right"),sQuery(id+"F0.wireOp",EDGE,"E1.top"),sQuery(id+"F0.wireOp",EDGE,"E1.right"),sQuery(id+"F0.wireOp",EDGE,"E3.top"),sQuery(id+"F0.wireOp",EDGE,"E3.left"),sQuery(id+"F0.wireOp",EDGE,"E3.right"),sQuery(id+"F0.wireOp",EDGE,"E4.top"),sQuery(id+"F0.wireOp",EDGE,"E4.right"),sQuery(id+"F0.wireOp",EDGE,"E5.trimOffspring")])],"isStart":false});
            var sketch = newSketch(context, id + "F26", { "sketchPlane" : qUnion([Q0])});
            skText(sketch, "E78", { "text": "NOVIEMBRE", "fontName": "OpenSans-Regular.ttf"});
            skPoint(sketch, "E79.orphan", {"position": v(53.92, 15.5) * mm});
            skPoint(sketch, "E80.end.orphan", {"position": v(1.08, -34.46) * mm});
            skPoint(sketch, "E81.orphan", {"position": v(-47.92, 15.5) * mm});
            skPoint(sketch, "E82.start.orphan", {"position": v(1.08, -17.46) * mm});
            skLineSegment(sketch, "E83.0", {"start": v(-42.5, 15.5) * mm, "end": v(48.5, 15.5) * mm});
            const initialGuessF26  = {"E78": [-0.03653, 0.0055, 1, 0, 0.01]};
            skSetInitialGuess(sketch, initialGuessF26);
            skSolve(sketch);
        }
        {
            var Q0;
            Q0=makeQuery(id+"F0.imprint","IMPRINT",FACE,{"disambiguationData":[TD([[makeQuery(id+"F0.imprint","IMPRINT",EDGE,{"derivedFrom":sQuery(id+"F0.wireOp",EDGE,"E0.bottom")}),-1.0]])]});
            extrude(context, id + "F27", {"entities" : qUnion([Q0]), "depth" : 3 * mm});
        }
        {
            var Q0;
            Q0=makeQuery(id+"F27.opExtrude","CAP_FACE",FACE,{"disambiguationData":[OSD([sQuery(id+"F0.wireOp",EDGE,"E0.bottom"),sQuery(id+"F0.wireOp",EDGE,"E0.top"),sQuery(id+"F0.wireOp",EDGE,"E0.left"),sQuery(id+"F0.wireOp",EDGE,"E0.right"),sQuery(id+"F0.wireOp",EDGE,"E1.top"),sQuery(id+"F0.wireOp",EDGE,"E1.right"),sQuery(id+"F0.wireOp",EDGE,"E3.top"),sQuery(id+"F0.wireOp",EDGE,"E3.left"),sQuery(id+"F0.wireOp",EDGE,"E3.right"),sQuery(id+"F0.wireOp",EDGE,"E4.top"),sQuery(id+"F0.wireOp",EDGE,"E4.right"),sQuery(id+"F0.wireOp",EDGE,"E5.trimOffspring")])],"isStart":false});
            var sketch = newSketch(context, id + "F28", { "sketchPlane" : qUnion([Q0])});
            skText(sketch, "E84", { "text": "DICIEMBRE", "fontName": "OpenSans-Regular.ttf"});
            skPoint(sketch, "E85.orphan", {"position": v(50.53, 15.5) * mm});
            skPoint(sketch, "E86.end.orphan", {"position": v(1.08, -34.46) * mm});
            skPoint(sketch, "E87.orphan", {"position": v(-44.53, 15.5) * mm});
            skPoint(sketch, "E88.start.orphan", {"position": v(1.08, -17.46) * mm});
            skLineSegment(sketch, "E89.0", {"start": v(-42.5, 15.5) * mm, "end": v(48.5, 15.5) * mm});
            const initialGuessF28  = {"E84": [-0.03313, 0.0055, 1, 0, 0.01]};
            skSetInitialGuess(sketch, initialGuessF28);
            skSolve(sketch);
        }
        {
            var Q0;
            Q0=makeQuery(id+"F28.imprint","IMPRINT",FACE,{"disambiguationData":[TD([[makeQuery(id+"F28.imprint","IMPRINT",EDGE,{"derivedFrom":sQuery(id+"F28.wireOp",EDGE,"E84.sketch_text.stroke-0")}),-1.0]])]});
            var Q1;
            Q1=makeQuery(id+"F28.imprint","IMPRINT",FACE,{"disambiguationData":[TD([[makeQuery(id+"F28.imprint","IMPRINT",EDGE,{"derivedFrom":sQuery(id+"F28.wireOp",EDGE,"E84.sketch_text.stroke-14")}),-1.0]])]});
            var Q2;
            Q2=makeQuery(id+"F28.imprint","IMPRINT",FACE,{"disambiguationData":[TD([[makeQuery(id+"F28.imprint","IMPRINT",EDGE,{"derivedFrom":sQuery(id+"F28.wireOp",EDGE,"E84.sketch_text.stroke-26")}),-1.0]])]});
            var Q3;
            Q3=makeQuery(id+"F28.imprint","IMPRINT",FACE,{"disambiguationData":[TD([[makeQuery(id+"F28.imprint","IMPRINT",EDGE,{"derivedFrom":sQuery(id+"F28.wireOp",EDGE,"E84.sketch_text.stroke-41")}),-1.0]])]});
            var Q4;
            Q4=makeQuery(id+"F28.imprint","IMPRINT",FACE,{"disambiguationData":[TD([[makeQuery(id+"F28.imprint","IMPRINT",EDGE,{"derivedFrom":sQuery(id+"F28.wireOp",EDGE,"E84.sketch_text.stroke-53")}),-1.0]])]});
            var Q5;
            Q5=makeQuery(id+"F28.imprint","IMPRINT",FACE,{"disambiguationData":[TD([[makeQuery(id+"F28.imprint","IMPRINT",EDGE,{"derivedFrom":sQuery(id+"F28.wireOp",EDGE,"E84.sketch_text.stroke-71")}),-1.0]])]});
            var Q6;
            Q6=makeQuery(id+"F28.imprint","IMPRINT",FACE,{"disambiguationData":[TD([[makeQuery(id+"F28.imprint","IMPRINT",EDGE,{"derivedFrom":sQuery(id+"F28.wireOp",EDGE,"E84.sketch_text.stroke-96")}),-1.0]])]});
            var Q7;
            Q7=makeQuery(id+"F28.imprint","IMPRINT",FACE,{"disambiguationData":[TD([[makeQuery(id+"F28.imprint","IMPRINT",EDGE,{"derivedFrom":sQuery(id+"F28.wireOp",EDGE,"E84.sketch_text.stroke-108")}),-1.0]])]});
            var Q8;
            Q8=makeQuery(id+"F28.imprint","IMPRINT",FACE,{"disambiguationData":[TD([[makeQuery(id+"F28.imprint","IMPRINT",EDGE,{"derivedFrom":sQuery(id+"F28.wireOp",EDGE,"E84.sketch_text.stroke-33")}),-1.0]])]});
            var Q9;
            Q9=makeQuery(id+"F28.imprint","IMPRINT",FACE,{"disambiguationData":[TD([[makeQuery(id+"F28.imprint","IMPRINT",EDGE,{"derivedFrom":sQuery(id+"F28.wireOp",EDGE,"E84.sketch_text.stroke-110")}),-1.0]])]});
            extrude(context, id + "F29", {"entities" : qUnion([Q0, Q1, Q2, Q3, Q4, Q5, Q6, Q7, Q8, Q9]), "operationType" : NewBodyOperationType.ADD, "depth" : 2 * mm});
        }
        {
            var Q0;
            Q0=makeQuery(id+"F26.imprint","IMPRINT",FACE,{"disambiguationData":[TD([[makeQuery(id+"F26.imprint","IMPRINT",EDGE,{"derivedFrom":sQuery(id+"F26.wireOp",EDGE,"E78.sketch_text.stroke-0")}),-1.0]])]});
            var Q1;
            Q1=makeQuery(id+"F26.imprint","IMPRINT",FACE,{"disambiguationData":[TD([[makeQuery(id+"F26.imprint","IMPRINT",EDGE,{"derivedFrom":sQuery(id+"F26.wireOp",EDGE,"E78.sketch_text.stroke-15")}),-1.0]])]});
            var Q2;
            Q2=makeQuery(id+"F26.imprint","IMPRINT",FACE,{"disambiguationData":[TD([[makeQuery(id+"F26.imprint","IMPRINT",EDGE,{"derivedFrom":sQuery(id+"F26.wireOp",EDGE,"E78.sketch_text.stroke-31")}),-1.0]])]});
            var Q3;
            Q3=makeQuery(id+"F26.imprint","IMPRINT",FACE,{"disambiguationData":[TD([[makeQuery(id+"F26.imprint","IMPRINT",EDGE,{"derivedFrom":sQuery(id+"F26.wireOp",EDGE,"E78.sketch_text.stroke-40")}),-1.0]])]});
            var Q4;
            Q4=makeQuery(id+"F26.imprint","IMPRINT",FACE,{"disambiguationData":[TD([[makeQuery(id+"F26.imprint","IMPRINT",EDGE,{"derivedFrom":sQuery(id+"F26.wireOp",EDGE,"E78.sketch_text.stroke-52")}),-1.0]])]});
            var Q5;
            Q5=makeQuery(id+"F26.imprint","IMPRINT",FACE,{"disambiguationData":[TD([[makeQuery(id+"F26.imprint","IMPRINT",EDGE,{"derivedFrom":sQuery(id+"F26.wireOp",EDGE,"E78.sketch_text.stroke-70")}),-1.0]])]});
            var Q6;
            Q6=makeQuery(id+"F26.imprint","IMPRINT",FACE,{"disambiguationData":[TD([[makeQuery(id+"F26.imprint","IMPRINT",EDGE,{"derivedFrom":sQuery(id+"F26.wireOp",EDGE,"E78.sketch_text.stroke-95")}),-1.0]])]});
            var Q7;
            Q7=makeQuery(id+"F26.imprint","IMPRINT",FACE,{"disambiguationData":[TD([[makeQuery(id+"F26.imprint","IMPRINT",EDGE,{"derivedFrom":sQuery(id+"F26.wireOp",EDGE,"E78.sketch_text.stroke-107")}),-1.0]])]});
            var Q8;
            Q8=makeQuery(id+"F26.imprint","IMPRINT",FACE,{"disambiguationData":[TD([[makeQuery(id+"F26.imprint","IMPRINT",EDGE,{"derivedFrom":sQuery(id+"F26.wireOp",EDGE,"E78.sketch_text.stroke-117")}),-1.0]])]});
            extrude(context, id + "F30", {"entities" : qUnion([Q0, Q1, Q2, Q3, Q4, Q5, Q6, Q7, Q8]), "operationType" : NewBodyOperationType.ADD, "depth" : 2 * mm});
        }
        {
            var Q0;
            Q0=makeQuery(id+"F24.imprint","IMPRINT",FACE,{"disambiguationData":[TD([[makeQuery(id+"F24.imprint","IMPRINT",EDGE,{"derivedFrom":sQuery(id+"F24.wireOp",EDGE,"E72.sketch_text.stroke-0")}),-1.0]])]});
            var Q1;
            Q1=makeQuery(id+"F24.imprint","IMPRINT",FACE,{"disambiguationData":[TD([[makeQuery(id+"F24.imprint","IMPRINT",EDGE,{"derivedFrom":sQuery(id+"F24.wireOp",EDGE,"E72.sketch_text.stroke-16")}),-1.0]])]});
            var Q2;
            Q2=makeQuery(id+"F24.imprint","IMPRINT",FACE,{"disambiguationData":[TD([[makeQuery(id+"F24.imprint","IMPRINT",EDGE,{"derivedFrom":sQuery(id+"F24.wireOp",EDGE,"E72.sketch_text.stroke-31")}),-1.0]])]});
            var Q3;
            Q3=makeQuery(id+"F24.imprint","IMPRINT",FACE,{"disambiguationData":[TD([[makeQuery(id+"F24.imprint","IMPRINT",EDGE,{"derivedFrom":sQuery(id+"F24.wireOp",EDGE,"E72.sketch_text.stroke-39")}),-1.0]])]});
            var Q4;
            Q4=makeQuery(id+"F24.imprint","IMPRINT",FACE,{"disambiguationData":[TD([[makeQuery(id+"F24.imprint","IMPRINT",EDGE,{"derivedFrom":sQuery(id+"F24.wireOp",EDGE,"E72.sketch_text.stroke-55")}),-1.0]])]});
            var Q5;
            Q5=makeQuery(id+"F24.imprint","IMPRINT",FACE,{"disambiguationData":[TD([[makeQuery(id+"F24.imprint","IMPRINT",EDGE,{"derivedFrom":sQuery(id+"F24.wireOp",EDGE,"E72.sketch_text.stroke-80")}),-1.0]])]});
            var Q6;
            Q6=makeQuery(id+"F24.imprint","IMPRINT",FACE,{"disambiguationData":[TD([[makeQuery(id+"F24.imprint","IMPRINT",EDGE,{"derivedFrom":sQuery(id+"F24.wireOp",EDGE,"E72.sketch_text.stroke-92")}),-1.0]])]});
            var Q7;
            Q7=makeQuery(id+"F24.imprint","IMPRINT",FACE,{"disambiguationData":[TD([[makeQuery(id+"F24.imprint","IMPRINT",EDGE,{"derivedFrom":sQuery(id+"F24.wireOp",EDGE,"E72.sketch_text.stroke-110")}),-1.0]])]});
            extrude(context, id + "F31", {"entities" : qUnion([Q0, Q1, Q2, Q3, Q4, Q5, Q6, Q7]), "operationType" : NewBodyOperationType.ADD, "depth" : 2 * mm});
        }
        {
            var Q0;
            Q0=makeQuery(id+"F22.imprint","IMPRINT",FACE,{"disambiguationData":[TD([[makeQuery(id+"F22.imprint","IMPRINT",EDGE,{"derivedFrom":sQuery(id+"F22.wireOp",EDGE,"E67.sketch_text.stroke-0")}),-1.0]])]});
            var Q1;
            Q1=makeQuery(id+"F22.imprint","IMPRINT",FACE,{"disambiguationData":[TD([[makeQuery(id+"F22.imprint","IMPRINT",EDGE,{"derivedFrom":sQuery(id+"F22.wireOp",EDGE,"E67.sketch_text.stroke-25")}),-1.0]])]});
            var Q2;
            Q2=makeQuery(id+"F22.imprint","IMPRINT",FACE,{"disambiguationData":[TD([[makeQuery(id+"F22.imprint","IMPRINT",EDGE,{"derivedFrom":sQuery(id+"F22.wireOp",EDGE,"E67.sketch_text.stroke-37")}),-1.0]])]});
            var Q3;
            Q3=makeQuery(id+"F22.imprint","IMPRINT",FACE,{"disambiguationData":[TD([[makeQuery(id+"F22.imprint","IMPRINT",EDGE,{"derivedFrom":sQuery(id+"F22.wireOp",EDGE,"E67.sketch_text.stroke-52")}),-1.0]])]});
            var Q4;
            Q4=makeQuery(id+"F22.imprint","IMPRINT",FACE,{"disambiguationData":[TD([[makeQuery(id+"F22.imprint","IMPRINT",EDGE,{"derivedFrom":sQuery(id+"F22.wireOp",EDGE,"E67.sketch_text.stroke-60")}),-1.0]])]});
            var Q5;
            Q5=makeQuery(id+"F22.imprint","IMPRINT",FACE,{"disambiguationData":[TD([[makeQuery(id+"F22.imprint","IMPRINT",EDGE,{"derivedFrom":sQuery(id+"F22.wireOp",EDGE,"E67.sketch_text.stroke-72")}),-1.0]])]});
            var Q6;
            Q6=makeQuery(id+"F22.imprint","IMPRINT",FACE,{"disambiguationData":[TD([[makeQuery(id+"F22.imprint","IMPRINT",EDGE,{"derivedFrom":sQuery(id+"F22.wireOp",EDGE,"E67.sketch_text.stroke-90")}),-1.0]])]});
            var Q7;
            Q7=makeQuery(id+"F22.imprint","IMPRINT",FACE,{"disambiguationData":[TD([[makeQuery(id+"F22.imprint","IMPRINT",EDGE,{"derivedFrom":sQuery(id+"F22.wireOp",EDGE,"E67.sketch_text.stroke-115")}),-1.0]])]});
            var Q8;
            Q8=makeQuery(id+"F22.imprint","IMPRINT",FACE,{"disambiguationData":[TD([[makeQuery(id+"F22.imprint","IMPRINT",EDGE,{"derivedFrom":sQuery(id+"F22.wireOp",EDGE,"E67.sketch_text.stroke-127")}),-1.0]])]});
            var Q9;
            Q9=makeQuery(id+"F22.imprint","IMPRINT",FACE,{"disambiguationData":[TD([[makeQuery(id+"F22.imprint","IMPRINT",EDGE,{"derivedFrom":sQuery(id+"F22.wireOp",EDGE,"E67.sketch_text.stroke-137")}),-1.0]])]});
            extrude(context, id + "F32", {"entities" : qUnion([Q0, Q1, Q2, Q3, Q4, Q5, Q6, Q7, Q8, Q9]), "operationType" : NewBodyOperationType.ADD, "depth" : 2 * mm});
        }
        {
            var Q0;
            Q0=makeQuery(id+"F20.imprint","IMPRINT",FACE,{"disambiguationData":[TD([[makeQuery(id+"F20.imprint","IMPRINT",EDGE,{"derivedFrom":sQuery(id+"F20.wireOp",EDGE,"E57.sketch_text.stroke-0")}),-1.0]])]});
            var Q1;
            Q1=makeQuery(id+"F20.imprint","IMPRINT",FACE,{"disambiguationData":[TD([[makeQuery(id+"F20.imprint","IMPRINT",EDGE,{"derivedFrom":sQuery(id+"F20.wireOp",EDGE,"E57.sketch_text.stroke-13")}),-1.0]])]});
            var Q2;
            Q2=makeQuery(id+"F20.imprint","IMPRINT",FACE,{"disambiguationData":[TD([[makeQuery(id+"F20.imprint","IMPRINT",EDGE,{"derivedFrom":sQuery(id+"F20.wireOp",EDGE,"E57.sketch_text.stroke-27")}),-1.0]])]});
            var Q3;
            Q3=makeQuery(id+"F20.imprint","IMPRINT",FACE,{"disambiguationData":[TD([[makeQuery(id+"F20.imprint","IMPRINT",EDGE,{"derivedFrom":sQuery(id+"F20.wireOp",EDGE,"E57.sketch_text.stroke-47")}),-1.0]])]});
            var Q4;
            Q4=makeQuery(id+"F20.imprint","IMPRINT",FACE,{"disambiguationData":[TD([[makeQuery(id+"F20.imprint","IMPRINT",EDGE,{"derivedFrom":sQuery(id+"F20.wireOp",EDGE,"E57.sketch_text.stroke-61")}),-1.0]])]});
            var Q5;
            Q5=makeQuery(id+"F20.imprint","IMPRINT",FACE,{"disambiguationData":[TD([[makeQuery(id+"F20.imprint","IMPRINT",EDGE,{"derivedFrom":sQuery(id+"F20.wireOp",EDGE,"E57.sketch_text.stroke-86")}),-1.0]])]});
            var Q6;
            Q6=makeQuery(id+"F20.imprint","IMPRINT",FACE,{"disambiguationData":[TD([[makeQuery(id+"F20.imprint","IMPRINT",EDGE,{"derivedFrom":sQuery(id+"F20.wireOp",EDGE,"E57.sketch_text.stroke-74")}),-1.0]])]});
            extrude(context, id + "F33", {"entities" : qUnion([Q0, Q1, Q2, Q3, Q4, Q5, Q6]), "operationType" : NewBodyOperationType.ADD, "depth" : 2 * mm});
        }
        {
            var Q0;
            Q0=makeQuery(id+"F18.imprint","IMPRINT",FACE,{"disambiguationData":[TD([[makeQuery(id+"F18.imprint","IMPRINT",EDGE,{"derivedFrom":sQuery(id+"F18.wireOp",EDGE,"E48.sketch_text.stroke-0")}),-1.0]])]});
            var Q1;
            Q1=makeQuery(id+"F18.imprint","IMPRINT",FACE,{"disambiguationData":[TD([[makeQuery(id+"F18.imprint","IMPRINT",EDGE,{"derivedFrom":sQuery(id+"F18.wireOp",EDGE,"E48.sketch_text.stroke-10")}),-1.0]])]});
            var Q2;
            Q2=makeQuery(id+"F18.imprint","IMPRINT",FACE,{"disambiguationData":[TD([[makeQuery(id+"F18.imprint","IMPRINT",EDGE,{"derivedFrom":sQuery(id+"F18.wireOp",EDGE,"E48.sketch_text.stroke-24")}),-1.0]])]});
            var Q3;
            Q3=makeQuery(id+"F18.imprint","IMPRINT",FACE,{"disambiguationData":[TD([[makeQuery(id+"F18.imprint","IMPRINT",EDGE,{"derivedFrom":sQuery(id+"F18.wireOp",EDGE,"E48.sketch_text.stroke-30")}),-1.0]])]});
            var Q4;
            Q4=makeQuery(id+"F18.imprint","IMPRINT",FACE,{"disambiguationData":[TD([[makeQuery(id+"F18.imprint","IMPRINT",EDGE,{"derivedFrom":sQuery(id+"F18.wireOp",EDGE,"E48.sketch_text.stroke-34")}),-1.0]])]});
            extrude(context, id + "F34", {"entities" : qUnion([Q0, Q1, Q2, Q3, Q4]), "operationType" : NewBodyOperationType.ADD, "depth" : 2 * mm});
        }
        {
            var Q0;
            Q0=makeQuery(id+"F16.imprint","IMPRINT",FACE,{"disambiguationData":[TD([[makeQuery(id+"F16.imprint","IMPRINT",EDGE,{"derivedFrom":sQuery(id+"F16.wireOp",EDGE,"E40.sketch_text.stroke-0")}),-1.0]])]});
            var Q1;
            Q1=makeQuery(id+"F16.imprint","IMPRINT",FACE,{"disambiguationData":[TD([[makeQuery(id+"F16.imprint","IMPRINT",EDGE,{"derivedFrom":sQuery(id+"F16.wireOp",EDGE,"E40.sketch_text.stroke-10")}),-1.0]])]});
            var Q2;
            Q2=makeQuery(id+"F16.imprint","IMPRINT",FACE,{"disambiguationData":[TD([[makeQuery(id+"F16.imprint","IMPRINT",EDGE,{"derivedFrom":sQuery(id+"F16.wireOp",EDGE,"E40.sketch_text.stroke-24")}),-1.0]])]});
            var Q3;
            Q3=makeQuery(id+"F16.imprint","IMPRINT",FACE,{"disambiguationData":[TD([[makeQuery(id+"F16.imprint","IMPRINT",EDGE,{"derivedFrom":sQuery(id+"F16.wireOp",EDGE,"E40.sketch_text.stroke-39")}),-1.0]])]});
            var Q4;
            Q4=makeQuery(id+"F16.imprint","IMPRINT",FACE,{"disambiguationData":[TD([[makeQuery(id+"F16.imprint","IMPRINT",EDGE,{"derivedFrom":sQuery(id+"F16.wireOp",EDGE,"E40.sketch_text.stroke-43")}),-1.0]])]});
            extrude(context, id + "F35", {"entities" : qUnion([Q0, Q1, Q2, Q3, Q4]), "operationType" : NewBodyOperationType.ADD, "depth" : 2 * mm});
        }
        {
            var Q0;
            Q0=makeQuery(id+"F14.imprint","IMPRINT",FACE,{"disambiguationData":[TD([[makeQuery(id+"F14.imprint","IMPRINT",EDGE,{"derivedFrom":sQuery(id+"F14.wireOp",EDGE,"E33.sketch_text.stroke-0")}),-1.0]])]});
            var Q1;
            Q1=makeQuery(id+"F14.imprint","IMPRINT",FACE,{"disambiguationData":[TD([[makeQuery(id+"F14.imprint","IMPRINT",EDGE,{"derivedFrom":sQuery(id+"F14.wireOp",EDGE,"E33.sketch_text.stroke-18")}),-1.0]])]});
            var Q2;
            Q2=makeQuery(id+"F14.imprint","IMPRINT",FACE,{"disambiguationData":[TD([[makeQuery(id+"F14.imprint","IMPRINT",EDGE,{"derivedFrom":sQuery(id+"F14.wireOp",EDGE,"E33.sketch_text.stroke-31")}),-1.0]])]});
            var Q3;
            Q3=makeQuery(id+"F14.imprint","IMPRINT",FACE,{"disambiguationData":[TD([[makeQuery(id+"F14.imprint","IMPRINT",EDGE,{"derivedFrom":sQuery(id+"F14.wireOp",EDGE,"E33.sketch_text.stroke-40")}),-1.0]])]});
            extrude(context, id + "F36", {"entities" : qUnion([Q0, Q1, Q2, Q3]), "operationType" : NewBodyOperationType.ADD, "depth" : 2 * mm});
        }
        {
            var Q0;
            Q0=makeQuery(id+"F0.imprint","IMPRINT",FACE,{"disambiguationData":[TD([[makeQuery(id+"F0.imprint","IMPRINT",EDGE,{"derivedFrom":sQuery(id+"F0.wireOp",EDGE,"E0.bottom")}),-1.0]])]});
            extrude(context, id + "F37", {"entities" : qUnion([Q0]), "depth" : 3 * mm});
        }
    });
